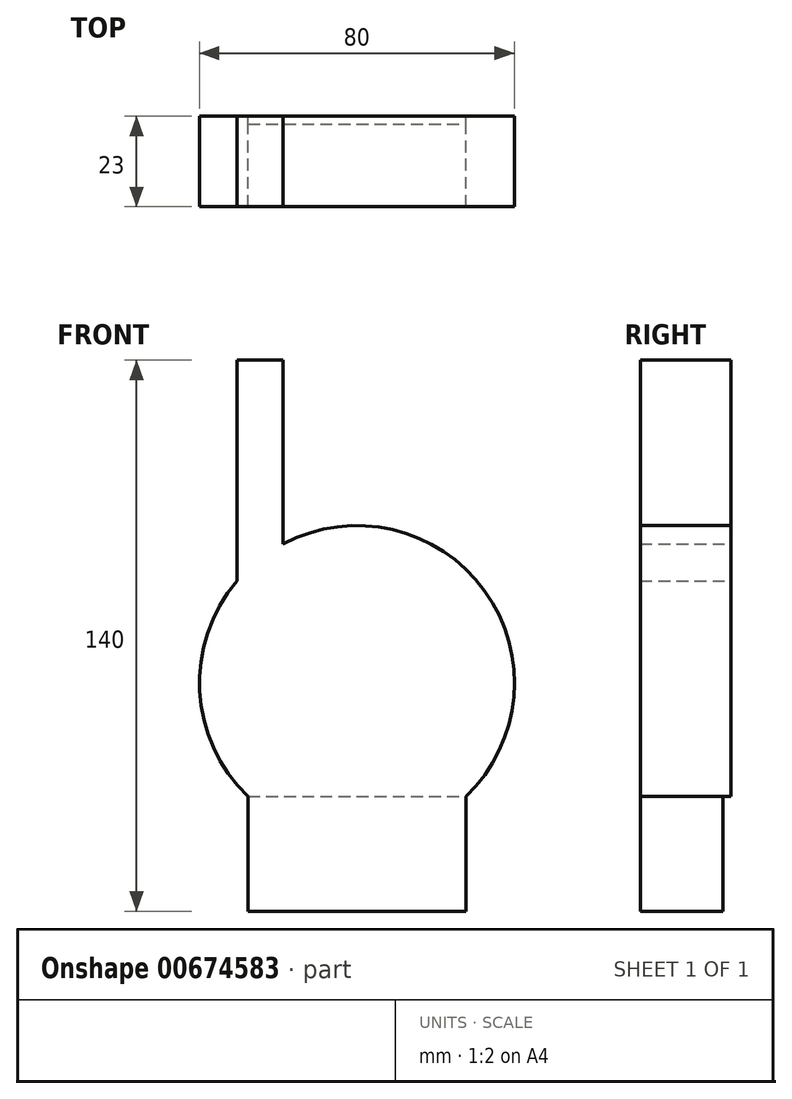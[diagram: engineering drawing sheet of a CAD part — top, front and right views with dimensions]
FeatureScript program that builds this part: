
annotation { "Feature Type Name" : "Feature", "Feature Type Description" : "" }
export const myFeature = defineFeature(function(context is Context, id is Id, definition is map)
    precondition{}
    {
        {
            var Q0;
            Q0=qCreatedBy(makeId("Front.planeOp"),FACE);
            var sketch = newSketch(context, id + "F0", { "sketchPlane" : qUnion([Q0])});
            skArc(sketch, "E0", {"start": v(58.7, -83.5) * mm, "mid": v(63.42, -31.2) * mm, "end": v(12.27, -19.3) * mm});
            skLineSegment(sketch, "E1", {"start": v(3.32, -83.5) * mm, "end": v(3.32, -112.64) * mm});
            skLineSegment(sketch, "E2", {"start": v(3.32, -112.64) * mm, "end": v(58.7, -112.64) * mm});
            skLineSegment(sketch, "E3", {"start": v(58.7, -112.64) * mm, "end": v(58.7, -83.5) * mm});
            skLineSegment(sketch, "E4", {"start": v(0.55, -28.7) * mm, "end": v(0.55, 27.36) * mm});
            skLineSegment(sketch, "E5", {"start": v(0.55, 27.36) * mm, "end": v(12.27, 27.36) * mm});
            skLineSegment(sketch, "E6", {"start": v(12.27, 27.36) * mm, "end": v(12.27, -19.3) * mm});
            skArc(sketch, "E7.trimOffspring", {"start": v(0.55, -28.7) * mm, "mid": v(-8.94, -56.66) * mm, "end": v(3.32, -83.5) * mm});
            skSolve(sketch);
        }
        {
            var Q0;
            Q0 = qSketchRegion(id + "F0", true);
            extrude(context, id + "F1", {"entities" : qUnion([Q0]), "depth" : 23 * mm, "offsetDistance" : 25 * mm});
        }
        {
            var Q0;
            Q0=makeQuery(id+"F1.opExtrude","CAP_FACE",FACE,{"disambiguationData":[OSD([sQuery(id+"F0.wireOp",EDGE,"E0"),sQuery(id+"F0.wireOp",EDGE,"E1"),sQuery(id+"F0.wireOp",EDGE,"E2"),sQuery(id+"F0.wireOp",EDGE,"E3"),sQuery(id+"F0.wireOp",EDGE,"E4"),sQuery(id+"F0.wireOp",EDGE,"E5"),sQuery(id+"F0.wireOp",EDGE,"E6"),sQuery(id+"F0.wireOp",EDGE,"E7.trimOffspring")])],"isStart":true});
            var sketch = newSketch(context, id + "F2", { "sketchPlane" : qUnion([Q0])});
            skLineSegment(sketch, "E8.bottom", {"start": v(-3.32, -112.64) * mm, "end": v(-58.7, -112.64) * mm});
            skLineSegment(sketch, "E8.top", {"start": v(-3.32, -83.5) * mm, "end": v(-58.7, -83.5) * mm});
            skLineSegment(sketch, "E8.left", {"start": v(-3.32, -112.64) * mm, "end": v(-3.32, -83.5) * mm});
            skLineSegment(sketch, "E8.right", {"start": v(-58.7, -112.64) * mm, "end": v(-58.7, -83.5) * mm});
            skSolve(sketch);
        }
        {
            var Q0;
            Q0 = qSketchRegion(id + "F2", true);
            extrude(context, id + "F3", {"entities" : qUnion([Q0]), "operationType" : NewBodyOperationType.REMOVE, "oppositeDirection" : true, "depth" : 2 * mm, "offsetDistance" : 25 * mm});
        }
    });
